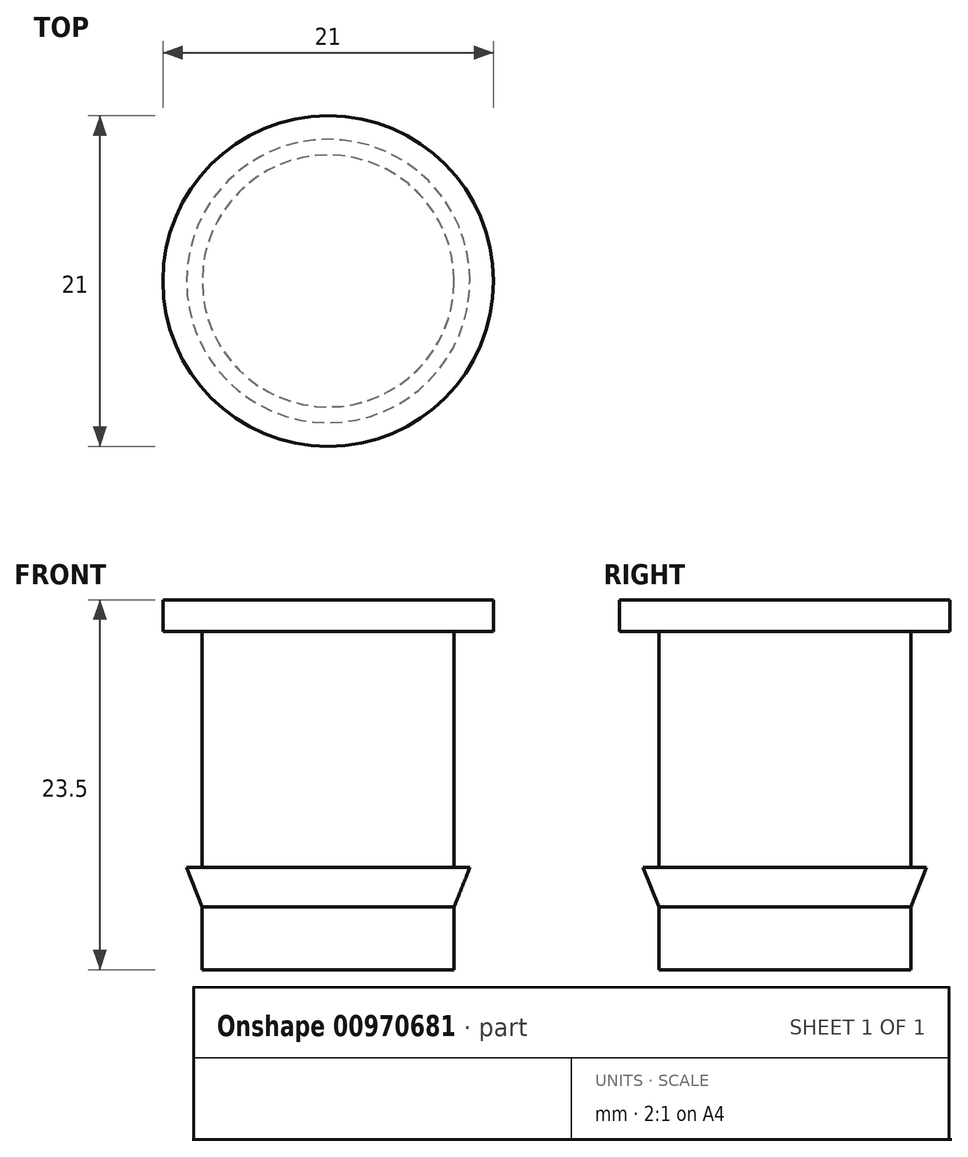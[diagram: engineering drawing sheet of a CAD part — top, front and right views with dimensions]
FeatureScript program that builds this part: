
annotation { "Feature Type Name" : "Feature", "Feature Type Description" : "" }
export const myFeature = defineFeature(function(context is Context, id is Id, definition is map)
    precondition{}
    {
        {
            var Q0;
            Q0=qCreatedBy(makeId("Front.planeOp"),FACE);
            var sketch = newSketch(context, id + "F0", { "sketchPlane" : qUnion([Q0])});
            skLineSegment(sketch, "E0", {"start": v(0, 0) * mm, "end": v(-8, 0) * mm});
            skLineSegment(sketch, "E1", {"start": v(-8, 0) * mm, "end": v(-8, 4) * mm});
            skLineSegment(sketch, "E2", {"start": v(-8, 6.5) * mm, "end": v(-8, 21.5) * mm});
            skLineSegment(sketch, "E3", {"start": v(-8, 6.5) * mm, "end": v(-9, 6.5) * mm});
            skLineSegment(sketch, "E4", {"start": v(-9, 6.5) * mm, "end": v(-8, 4) * mm});
            skLineSegment(sketch, "E5", {"start": v(-8, 21.5) * mm, "end": v(-10.5, 21.5) * mm});
            skLineSegment(sketch, "E6", {"start": v(-10.5, 21.5) * mm, "end": v(-10.5, 23.5) * mm});
            skLineSegment(sketch, "E7", {"start": v(-10.5, 23.5) * mm, "end": v(0, 23.5) * mm});
            skLineSegment(sketch, "E8", {"start": v(0, 23.5) * mm, "end": v(0, 0) * mm});
            skSolve(sketch);
        }
        {
            var Q0;
            Q0 = qSketchRegion(id + "F0", true);
            var Q1;
            Q1=sQuery(id+"F0.wireOp",EDGE,"E8");
            revolve(context, id + "F1", {"surfaceOperationType" : NewSurfaceOperationType.NEW, "entities" : qUnion([Q0]), "axis" : qUnion([Q1]), "revolveType" : RevolveType.FULL});
        }
    });
